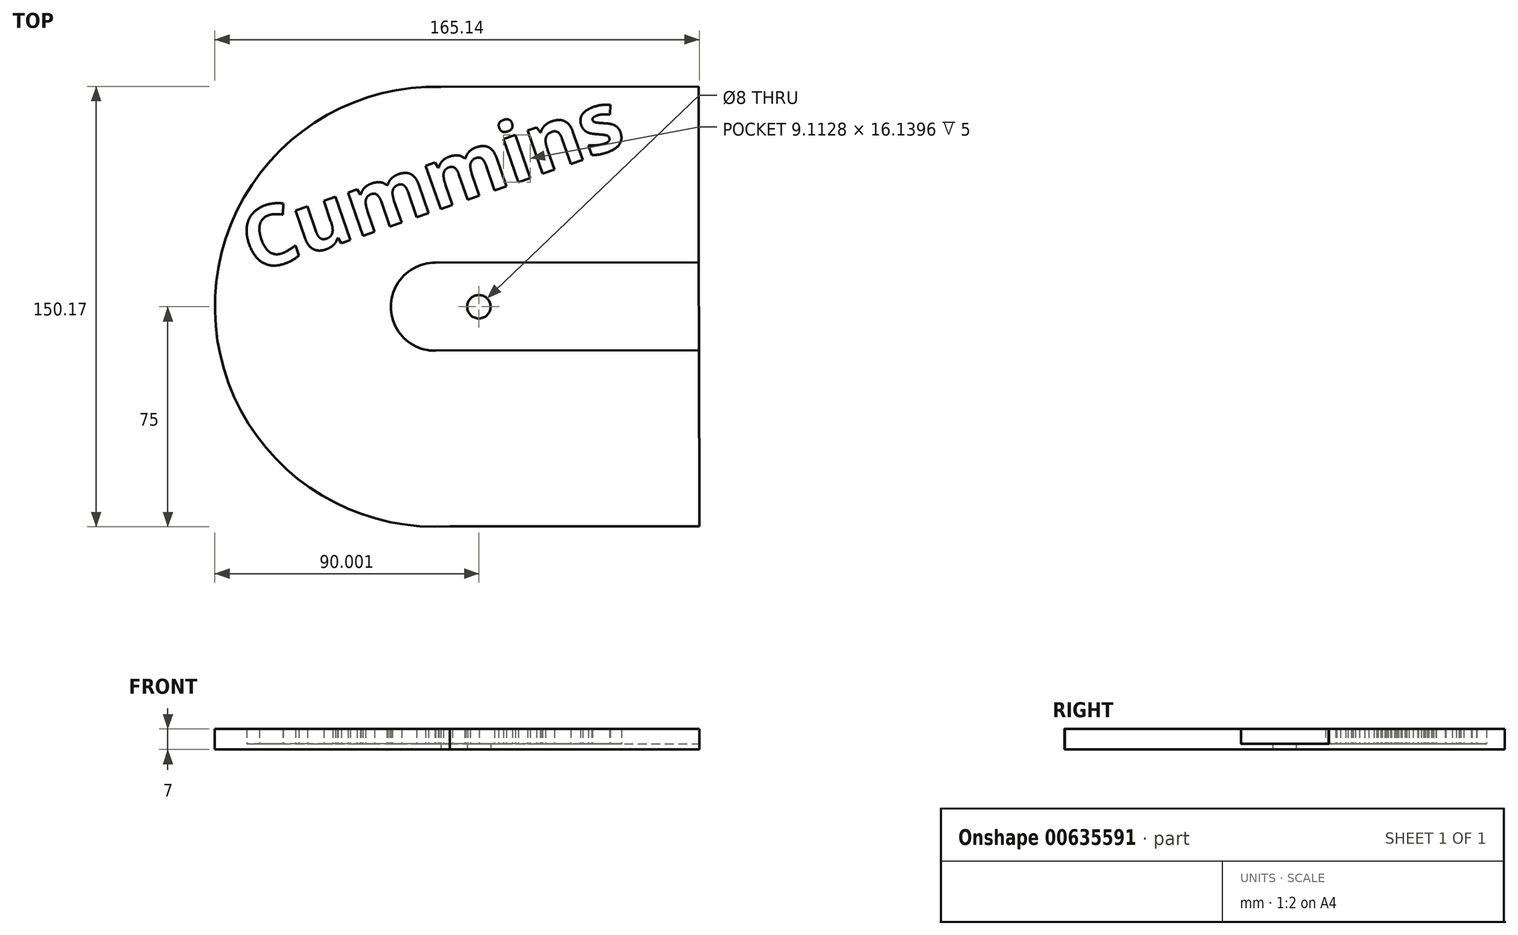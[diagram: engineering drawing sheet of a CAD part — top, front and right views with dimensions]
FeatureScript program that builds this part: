
annotation { "Feature Type Name" : "Feature", "Feature Type Description" : "" }
export const myFeature = defineFeature(function(context is Context, id is Id, definition is map)
    precondition{}
    {
        {
            var Q0;
            Q0=qCreatedBy(makeId("Top.planeOp"),FACE);
            var sketch = newSketch(context, id + "F0", { "sketchPlane" : qUnion([Q0])});
            skArc(sketch, "E0", {"start": v(-127.13, 74.97) * mm, "mid": v(-204.2, -1.5) * mm, "end": v(-124.13, -74.83) * mm});
            skLineSegment(sketch, "E1", {"start": v(-39.07, -74.83) * mm, "end": v(-134.3, -74.83) * mm});
            skLineSegment(sketch, "E2", {"start": v(-39.35, 75.17) * mm, "end": v(-131.63, 74.96) * mm});
            skLineSegment(sketch, "E3", {"start": v(-39.35, 75.17) * mm, "end": v(-39.24, 15.17) * mm});
            skArc(sketch, "E4", {"start": v(-129, 15) * mm, "mid": v(-144.2, 0) * mm, "end": v(-129, -15) * mm});
            skLineSegment(sketch, "E5", {"start": v(-129, 15) * mm, "end": v(-39.24, 15.17) * mm});
            skLineSegment(sketch, "E6", {"start": v(-129, -15) * mm, "end": v(-39.18, -14.83) * mm});
            skLineSegment(sketch, "E7.trimOffspring", {"start": v(-39.18, -14.83) * mm, "end": v(-39.07, -74.83) * mm});
            skText(sketch, "E8", { "text": "Cummins", "fontName": "OpenSans-Bold.ttf"});
            skPoint(sketch, "E9", {"position": v(-69.35, 75.1) * mm});
            const initialGuessF0  = {"E8": [-0.19085, 0.01141, 0.94532, 0.32614, 0.02058]};
            skSetInitialGuess(sketch, initialGuessF0);
            skSolve(sketch);
        }
        {
            var Q0;
            {var subQ3=sQuery(id+"F0.wireOp",EDGE,"E3");Q0=makeQuery(id+"F0.imprint","IMPRINT",FACE,{"disambiguationData":[TD([[makeQuery(id+"F0.imprint","IMPRINT",EDGE,{"derivedFrom":subQ3}),-1.0]])]});}
            var Q1;
            Q1 = qSketchRegion(id + "F0", true);
            extrude(context, id + "F1", {"entities" : qUnion([Q0, Q1]), "depth" : 5 * mm, "offsetDistance" : 25 * mm});
        }
        {
            var Q0;
            Q0=makeQuery(id+"F1.opExtrude","CAP_FACE",FACE,{"disambiguationData":[OSD([sQuery(id+"F0.wireOp",EDGE,"E0"),sQuery(id+"F0.wireOp",EDGE,"E1"),sQuery(id+"F0.wireOp",EDGE,"E2"),sQuery(id+"F0.wireOp",EDGE,"E3"),sQuery(id+"F0.wireOp",EDGE,"E4"),sQuery(id+"F0.wireOp",EDGE,"E5"),sQuery(id+"F0.wireOp",EDGE,"E6"),sQuery(id+"F0.wireOp",EDGE,"E7.trimOffspring"),sQuery(id+"F0.wireOp",EDGE,"E8.sketch_text.stroke-0"),sQuery(id+"F0.wireOp",EDGE,"E8.sketch_text.stroke-1"),sQuery(id+"F0.wireOp",EDGE,"E8.sketch_text.stroke-2"),sQuery(id+"F0.wireOp",EDGE,"E8.sketch_text.stroke-3"),sQuery(id+"F0.wireOp",EDGE,"E8.sketch_text.stroke-4"),sQuery(id+"F0.wireOp",EDGE,"E8.sketch_text.stroke-5"),sQuery(id+"F0.wireOp",EDGE,"E8.sketch_text.stroke-6"),sQuery(id+"F0.wireOp",EDGE,"E8.sketch_text.stroke-7"),sQuery(id+"F0.wireOp",EDGE,"E8.sketch_text.stroke-8"),sQuery(id+"F0.wireOp",EDGE,"E8.sketch_text.stroke-9"),sQuery(id+"F0.wireOp",EDGE,"E8.sketch_text.stroke-10"),sQuery(id+"F0.wireOp",EDGE,"E8.sketch_text.stroke-11"),sQuery(id+"F0.wireOp",EDGE,"E8.sketch_text.stroke-12"),sQuery(id+"F0.wireOp",EDGE,"E8.sketch_text.stroke-13"),sQuery(id+"F0.wireOp",EDGE,"E8.sketch_text.stroke-14"),sQuery(id+"F0.wireOp",EDGE,"E8.sketch_text.stroke-15"),sQuery(id+"F0.wireOp",EDGE,"E8.sketch_text.stroke-16"),sQuery(id+"F0.wireOp",EDGE,"E8.sketch_text.stroke-17"),sQuery(id+"F0.wireOp",EDGE,"E8.sketch_text.stroke-18"),sQuery(id+"F0.wireOp",EDGE,"E8.sketch_text.stroke-19"),sQuery(id+"F0.wireOp",EDGE,"E8.sketch_text.stroke-20"),sQuery(id+"F0.wireOp",EDGE,"E8.sketch_text.stroke-21"),sQuery(id+"F0.wireOp",EDGE,"E8.sketch_text.stroke-22"),sQuery(id+"F0.wireOp",EDGE,"E8.sketch_text.stroke-23"),sQuery(id+"F0.wireOp",EDGE,"E8.sketch_text.stroke-24"),sQuery(id+"F0.wireOp",EDGE,"E8.sketch_text.stroke-25"),sQuery(id+"F0.wireOp",EDGE,"E8.sketch_text.stroke-26"),sQuery(id+"F0.wireOp",EDGE,"E8.sketch_text.stroke-27"),sQuery(id+"F0.wireOp",EDGE,"E8.sketch_text.stroke-28"),sQuery(id+"F0.wireOp",EDGE,"E8.sketch_text.stroke-29"),sQuery(id+"F0.wireOp",EDGE,"E8.sketch_text.stroke-30"),sQuery(id+"F0.wireOp",EDGE,"E8.sketch_text.stroke-31"),sQuery(id+"F0.wireOp",EDGE,"E8.sketch_text.stroke-32"),sQuery(id+"F0.wireOp",EDGE,"E8.sketch_text.stroke-33"),sQuery(id+"F0.wireOp",EDGE,"E8.sketch_text.stroke-34"),sQuery(id+"F0.wireOp",EDGE,"E8.sketch_text.stroke-35"),sQuery(id+"F0.wireOp",EDGE,"E8.sketch_text.stroke-36"),sQuery(id+"F0.wireOp",EDGE,"E8.sketch_text.stroke-37"),sQuery(id+"F0.wireOp",EDGE,"E8.sketch_text.stroke-38"),sQuery(id+"F0.wireOp",EDGE,"E8.sketch_text.stroke-39"),sQuery(id+"F0.wireOp",EDGE,"E8.sketch_text.stroke-40"),sQuery(id+"F0.wireOp",EDGE,"E8.sketch_text.stroke-41"),sQuery(id+"F0.wireOp",EDGE,"E8.sketch_text.stroke-42"),sQuery(id+"F0.wireOp",EDGE,"E8.sketch_text.stroke-43"),sQuery(id+"F0.wireOp",EDGE,"E8.sketch_text.stroke-44"),sQuery(id+"F0.wireOp",EDGE,"E8.sketch_text.stroke-45"),sQuery(id+"F0.wireOp",EDGE,"E8.sketch_text.stroke-46"),sQuery(id+"F0.wireOp",EDGE,"E8.sketch_text.stroke-47"),sQuery(id+"F0.wireOp",EDGE,"E8.sketch_text.stroke-48"),sQuery(id+"F0.wireOp",EDGE,"E8.sketch_text.stroke-49"),sQuery(id+"F0.wireOp",EDGE,"E8.sketch_text.stroke-50"),sQuery(id+"F0.wireOp",EDGE,"E8.sketch_text.stroke-51"),sQuery(id+"F0.wireOp",EDGE,"E8.sketch_text.stroke-52"),sQuery(id+"F0.wireOp",EDGE,"E8.sketch_text.stroke-53"),sQuery(id+"F0.wireOp",EDGE,"E8.sketch_text.stroke-54"),sQuery(id+"F0.wireOp",EDGE,"E8.sketch_text.stroke-55"),sQuery(id+"F0.wireOp",EDGE,"E8.sketch_text.stroke-56"),sQuery(id+"F0.wireOp",EDGE,"E8.sketch_text.stroke-57"),sQuery(id+"F0.wireOp",EDGE,"E8.sketch_text.stroke-58"),sQuery(id+"F0.wireOp",EDGE,"E8.sketch_text.stroke-59"),sQuery(id+"F0.wireOp",EDGE,"E8.sketch_text.stroke-60"),sQuery(id+"F0.wireOp",EDGE,"E8.sketch_text.stroke-61"),sQuery(id+"F0.wireOp",EDGE,"E8.sketch_text.stroke-62"),sQuery(id+"F0.wireOp",EDGE,"E8.sketch_text.stroke-63"),sQuery(id+"F0.wireOp",EDGE,"E8.sketch_text.stroke-64"),sQuery(id+"F0.wireOp",EDGE,"E8.sketch_text.stroke-65"),sQuery(id+"F0.wireOp",EDGE,"E8.sketch_text.stroke-66"),sQuery(id+"F0.wireOp",EDGE,"E8.sketch_text.stroke-67"),sQuery(id+"F0.wireOp",EDGE,"E8.sketch_text.stroke-68"),sQuery(id+"F0.wireOp",EDGE,"E8.sketch_text.stroke-69"),sQuery(id+"F0.wireOp",EDGE,"E8.sketch_text.stroke-70"),sQuery(id+"F0.wireOp",EDGE,"E8.sketch_text.stroke-71"),sQuery(id+"F0.wireOp",EDGE,"E8.sketch_text.stroke-72"),sQuery(id+"F0.wireOp",EDGE,"E8.sketch_text.stroke-73"),sQuery(id+"F0.wireOp",EDGE,"E8.sketch_text.stroke-74"),sQuery(id+"F0.wireOp",EDGE,"E8.sketch_text.stroke-75"),sQuery(id+"F0.wireOp",EDGE,"E8.sketch_text.stroke-76"),sQuery(id+"F0.wireOp",EDGE,"E8.sketch_text.stroke-77"),sQuery(id+"F0.wireOp",EDGE,"E8.sketch_text.stroke-78"),sQuery(id+"F0.wireOp",EDGE,"E8.sketch_text.stroke-79"),sQuery(id+"F0.wireOp",EDGE,"E8.sketch_text.stroke-80"),sQuery(id+"F0.wireOp",EDGE,"E8.sketch_text.stroke-81"),sQuery(id+"F0.wireOp",EDGE,"E8.sketch_text.stroke-82"),sQuery(id+"F0.wireOp",EDGE,"E8.sketch_text.stroke-83"),sQuery(id+"F0.wireOp",EDGE,"E8.sketch_text.stroke-84"),sQuery(id+"F0.wireOp",EDGE,"E8.sketch_text.stroke-85"),sQuery(id+"F0.wireOp",EDGE,"E8.sketch_text.stroke-86"),sQuery(id+"F0.wireOp",EDGE,"E8.sketch_text.stroke-87"),sQuery(id+"F0.wireOp",EDGE,"E8.sketch_text.stroke-88"),sQuery(id+"F0.wireOp",EDGE,"E8.sketch_text.stroke-89"),sQuery(id+"F0.wireOp",EDGE,"E8.sketch_text.stroke-90"),sQuery(id+"F0.wireOp",EDGE,"E8.sketch_text.stroke-91"),sQuery(id+"F0.wireOp",EDGE,"E8.sketch_text.stroke-92"),sQuery(id+"F0.wireOp",EDGE,"E8.sketch_text.stroke-93"),sQuery(id+"F0.wireOp",EDGE,"E8.sketch_text.stroke-94"),sQuery(id+"F0.wireOp",EDGE,"E8.sketch_text.stroke-95"),sQuery(id+"F0.wireOp",EDGE,"E8.sketch_text.stroke-96"),sQuery(id+"F0.wireOp",EDGE,"E8.sketch_text.stroke-97"),sQuery(id+"F0.wireOp",EDGE,"E8.sketch_text.stroke-98"),sQuery(id+"F0.wireOp",EDGE,"E8.sketch_text.stroke-99"),sQuery(id+"F0.wireOp",EDGE,"E8.sketch_text.stroke-100"),sQuery(id+"F0.wireOp",EDGE,"E8.sketch_text.stroke-101"),sQuery(id+"F0.wireOp",EDGE,"E8.sketch_text.stroke-102"),sQuery(id+"F0.wireOp",EDGE,"E8.sketch_text.stroke-103"),sQuery(id+"F0.wireOp",EDGE,"E8.sketch_text.stroke-104"),sQuery(id+"F0.wireOp",EDGE,"E8.sketch_text.stroke-105"),sQuery(id+"F0.wireOp",EDGE,"E8.sketch_text.stroke-106"),sQuery(id+"F0.wireOp",EDGE,"E8.sketch_text.stroke-107"),sQuery(id+"F0.wireOp",EDGE,"E8.sketch_text.stroke-108"),sQuery(id+"F0.wireOp",EDGE,"E8.sketch_text.stroke-109"),sQuery(id+"F0.wireOp",EDGE,"E8.sketch_text.stroke-110"),sQuery(id+"F0.wireOp",EDGE,"E8.sketch_text.stroke-111"),sQuery(id+"F0.wireOp",EDGE,"E8.sketch_text.stroke-112"),sQuery(id+"F0.wireOp",EDGE,"E8.sketch_text.stroke-113"),sQuery(id+"F0.wireOp",EDGE,"E8.sketch_text.stroke-114"),sQuery(id+"F0.wireOp",EDGE,"E8.sketch_text.stroke-115"),sQuery(id+"F0.wireOp",EDGE,"E8.sketch_text.stroke-116"),sQuery(id+"F0.wireOp",EDGE,"E8.sketch_text.stroke-117"),sQuery(id+"F0.wireOp",EDGE,"E8.sketch_text.stroke-118"),sQuery(id+"F0.wireOp",EDGE,"E8.sketch_text.stroke-119"),sQuery(id+"F0.wireOp",EDGE,"E8.sketch_text.stroke-120"),sQuery(id+"F0.wireOp",EDGE,"E8.sketch_text.stroke-121"),sQuery(id+"F0.wireOp",EDGE,"E8.sketch_text.stroke-122"),sQuery(id+"F0.wireOp",EDGE,"E8.sketch_text.stroke-123"),sQuery(id+"F0.wireOp",EDGE,"E8.sketch_text.stroke-124"),sQuery(id+"F0.wireOp",EDGE,"E8.sketch_text.stroke-125"),sQuery(id+"F0.wireOp",EDGE,"E8.sketch_text.stroke-126"),sQuery(id+"F0.wireOp",EDGE,"E8.sketch_text.stroke-127"),sQuery(id+"F0.wireOp",EDGE,"E8.sketch_text.stroke-128"),sQuery(id+"F0.wireOp",EDGE,"E8.sketch_text.stroke-129"),sQuery(id+"F0.wireOp",EDGE,"E8.sketch_text.stroke-130"),sQuery(id+"F0.wireOp",EDGE,"E8.sketch_text.stroke-131"),sQuery(id+"F0.wireOp",EDGE,"E8.sketch_text.stroke-132"),sQuery(id+"F0.wireOp",EDGE,"E8.sketch_text.stroke-133"),sQuery(id+"F0.wireOp",EDGE,"E8.sketch_text.stroke-134")])],"isStart":true});
            var sketch = newSketch(context, id + "F2", { "sketchPlane" : qUnion([Q0])});
            skLineSegment(sketch, "E10.0", {"start": v(-39.35, -75.17) * mm, "end": v(-127.13, -74.97) * mm});
            skArc(sketch, "E11.0", {"start": v(-127.13, -74.97) * mm, "mid": v(-204.2, 1.5) * mm, "end": v(-124.13, 74.83) * mm});
            skLineSegment(sketch, "E12.0", {"start": v(-39.07, 74.83) * mm, "end": v(-124.13, 74.83) * mm});
            skLineSegment(sketch, "E13.0", {"start": v(-39.18, 14.83) * mm, "end": v(-39.07, 74.83) * mm});
            skLineSegment(sketch, "E14.0", {"start": v(-39.35, -75.17) * mm, "end": v(-39.24, -15.17) * mm});
            skLineSegment(sketch, "E15", {"start": v(-39.24, -15.17) * mm, "end": v(-39.18, 14.83) * mm});
            skSolve(sketch);
        }
        {
            var Q0;
            Q0 = qSketchRegion(id + "F2", true);
            extrude(context, id + "F3", {"entities" : qUnion([Q0]), "operationType" : NewBodyOperationType.ADD, "depth" : 2 * mm, "offsetDistance" : 25 * mm});
        }
        {
            var Q0;
            Q0=makeQuery(id+"F3.opExtrude","CAP_FACE",FACE,{"disambiguationData":[OSD([sQuery(id+"F2.wireOp",EDGE,"E10.0"),sQuery(id+"F2.wireOp",EDGE,"E11.0"),sQuery(id+"F2.wireOp",EDGE,"E12.0"),sQuery(id+"F2.wireOp",EDGE,"E13.0"),sQuery(id+"F2.wireOp",EDGE,"E14.0"),sQuery(id+"F2.wireOp",EDGE,"E15")])],"isStart":false});
            var sketch = newSketch(context, id + "F4", { "sketchPlane" : qUnion([Q0])});
            skCircle(sketch, "E16", {"center": v(-114.2, 0) * mm, "radius": 4 * mm});
            skSolve(sketch);
        }
        {
            var Q0;
            Q0 = qSketchRegion(id + "F4", true);
            extrude(context, id + "F5", {"entities" : qUnion([Q0]), "operationType" : NewBodyOperationType.REMOVE, "endBound" : BoundingType.UP_TO_NEXT, "oppositeDirection" : true, "depth" : 25 * mm, "offsetDistance" : 25 * mm});
        }
    });
